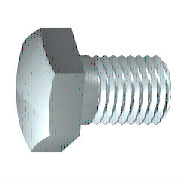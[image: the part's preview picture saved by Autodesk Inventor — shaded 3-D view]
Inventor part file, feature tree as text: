
AUTODESK INVENTOR PART (.ipt)
format: ipt  version: 2021 (Build 250183000, 183)  size: 193,536 bytes
history: native  units: mm (DEFAULTED — no unit token found)
features: sketch x3, extrude x1, chamfer x1, plane x1
ambient origin geometry x7: Origin, YZ Plane, XZ Plane, X Axis, Y Axis, Z Axis, Center Point
bodies: Solid1 (feature_tree), Body (feature_tree)
feature tree (6):
  extrude  "Head"  Depth=54.0mm
  chamfer  "Chamfer1"  Distance=14.2mm
  plane  "Work Plane1"
  sketch  "Sketch1"  dims[d0=75.0mm d1=54.0mm]
  sketch  "Sketch2"  dims[d2=24.0mm]
  sketch  "Sketch4"  dims[d12=90.0deg d3=14.2mm d4=0.0mm d5=30.0deg d21=90.0deg d6=1.84035mm d7=1.84045mm d8=0.0mm d9=0.8001mm d10=33.6mm d11=36.0mm d13=1.84045mm d14=24.0mm d15=54.0mm d16=0.0mm d19=36.0mm d55=45.0deg d57=0.0mm d58=0.0mm]
